# Revit family: oventrop_hydrocontrol-vpr_1060151-62rfa
name_source: partatom
category: Арматура трубопроводов
revit_build: Autodesk Revit 2017 (Build: 20160225_1515(x64)
units: mm (PartAtom-declared; Revit-internal decimal feet)

## family parameters
Всегда вертикально = Да
Заголовок OmniClass = Adjusting/Controlling Valves for Liquid Services
На основе рабочей плоскости = Нет
Номер OmniClass = 23.65.55.14.17
Общий = Нет
При загрузке вырезать с полостями = Нет
Размер круглого соединителя = Использовать радиус
Тип детали = Клапан - Вставляется

## types (7) — shared parameters
Angle = 50.00°
Article Description = Bronze double regulating and commissioning valves
Article Type = Hydrocontrol VPR 10601
Black = Color RGB 35-35-35
Bronze = Color RGB 156-122-90
Custom = Нет
EMCS Version = 2.0
ETIM Article Class = EC011463
Family Version = 10.14
Hb4 = 18 мм
Hb5 = 3 мм
Hlp1 = 22 мм
IFCExportAs = IfcValveType
IFCExportType = PRESSUREREDUCING
Lgt2 = 11 мм
MEPcontent Class = VALVE_BALANCING
Manufacturer URL = http://www.oventrop.de
Pressure Drop = 0.0 Па
Product Line = Oventrop
Revit Version = 2015
r1 = 2 мм
r2 = 3 мм
Группа модели = Hydrocontrol VPR 10601
Изготовитель = Oventrop
Описание = Bronze double regulating and commissioning valves

## per-type parameters (varying)
| type | Diameter | Dim_l | GTIN | Hb1 | Hb2 | Hb3 | Hb6 | Height | L2 | Lgt1 | Manufacturer Art. No. | NutDimension | PressConnection_Dimension | Rad1 | Rad2 | Rad3 | Rad4 | Rad5 | Radius | SW2 | URL | e2 | e3 | t |
| DN 40-42mm | 42 мм | 120 мм | 4026755344318 | 154 мм | 50 мм | 5 мм | 66 мм | 138 мм | 9 мм | 21 мм | 1060160 | 55 мм | 38 мм | 22 мм | 20 мм | 23 мм | 25 мм | 27 мм | 21 мм | 64 мм | www.stabiplan.com | 5 мм | 2 мм | 19 мм |
| DN 50-54mm | 54 мм | 150 мм | 4026755344325 | 167 мм | 50 мм | 15 мм | 76 мм | 148 мм | 13 мм | 28 мм | 1060162 | 70 мм | 43 мм | 30 мм | 28 мм | 31 мм | 33 мм | 35 мм | 27 мм | 81 мм | www.stabiplan.com | 5 мм | 3 мм | 26 мм |
| DN 32-35mm | 35 мм | 110 мм | 4026755344301 | 151 мм | 50 мм | 1 мм | 63 мм | 136 мм | 8 мм | 21 мм | 1060158 | 50 мм | 32 мм | 19 мм | 17 мм | 20 мм | 22 мм | 24 мм | 18 мм | 58 мм | www.stabiplan.com | 5 мм | 2 мм | 19 мм |
| DN 25-28mm | 28 мм | 98 мм | 4026755344295 | 129 мм | 50 мм | 13 мм | 81 мм | 119 мм | 6 мм | 19 мм | 1060156 | 41 мм | 27 мм | 16 мм | 14 мм | 16 мм | 19 мм | 21 мм | 14 мм | 47 мм | www.stabiplan.com | 4 мм | 2 мм | 17 мм |
| DN 20-22mm | 22 мм | 84 мм | 4026755344288 | 125 мм | 23 мм | 11 мм | 45 мм | 116 мм | 5 мм | 17 мм | 1060154 | 32 мм | 24 мм | 13 мм | 11 мм | 13 мм | 16 мм | 18 мм | 11 мм | 37 мм | www.stabiplan.com | 4 мм | 2 мм | 15 мм |
| DN 15-18mm | 18 мм | 80 мм | 4026755344271 | 122 мм | 21 мм | 15 мм | 48 мм | 114 мм | 3 мм | 15 мм | 1060152 | 27 мм | 20 мм | 10 мм | 8 мм | 10 мм | 13 мм | 15 мм | 9 мм | 31 мм | http://file-system.ru | 3 мм | 1 мм | 13 мм |
| DN 15-15mm | 15 мм | 80 мм | 4026755344264 | 122 мм | 19 мм | 15 мм | 46 мм | 114 мм | 3 мм | 15 мм | 1060151 | 27 мм | 18 мм | 10 мм | 8 мм | 10 мм | 13 мм | 15 мм | 8 мм | 31 мм | www.stabiplan.com | 3 мм | 1 мм | 13 мм |

## geometry (parser evidence)
native form markers: Sweep x2
no freeform markers — native parametric forms only
